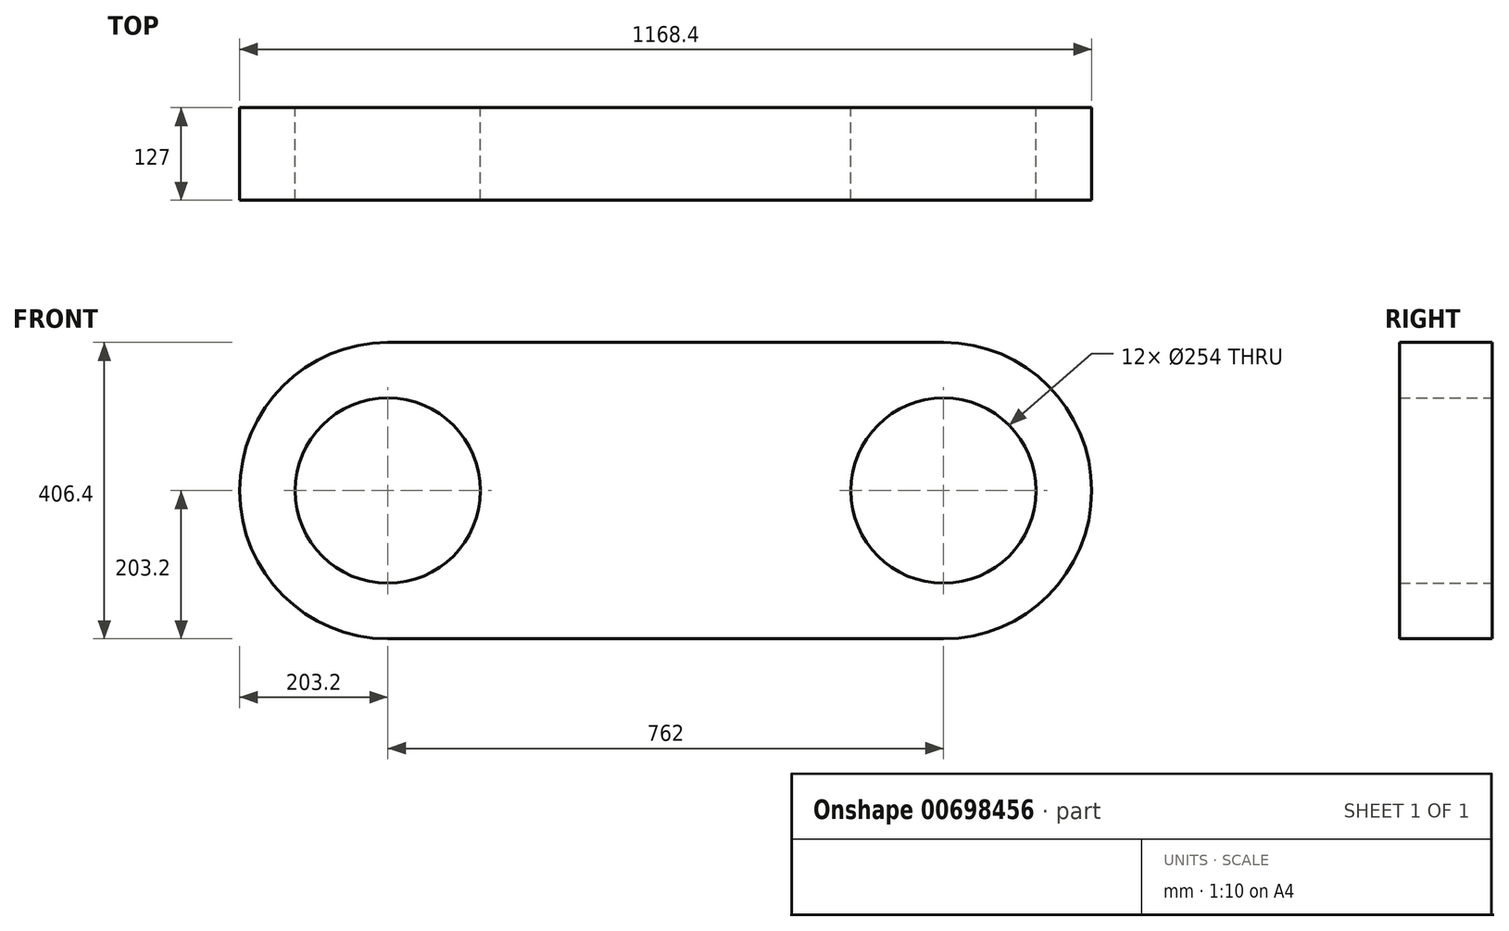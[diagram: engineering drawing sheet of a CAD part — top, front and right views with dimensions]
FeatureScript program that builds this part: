
annotation { "Feature Type Name" : "Feature", "Feature Type Description" : "" }
export const myFeature = defineFeature(function(context is Context, id is Id, definition is map)
    precondition{}
    {
        {
            var Q0;
            Q0=qCreatedBy(makeId("Front.planeOp"),FACE);
            var sketch = newSketch(context, id + "F0", { "sketchPlane" : qUnion([Q0])});
            skLineSegment(sketch, "E0.bottom", {"start": v(-381, 203.2) * mm, "end": v(381, 203.2) * mm});
            skLineSegment(sketch, "E0.top", {"start": v(-381, -203.2) * mm, "end": v(381, -203.2) * mm});
            skArc(sketch, "E1", {"start": v(-381, 203.2) * mm, "mid": v(-584.2, 0) * mm, "end": v(-381, -203.2) * mm});
            skArc(sketch, "E2", {"start": v(381, -203.2) * mm, "mid": v(584.2, 0) * mm, "end": v(381, 203.2) * mm});
            skCircle(sketch, "E3", {"center": v(381, 0) * mm, "radius": 127 * mm});
            skCircle(sketch, "E4", {"center": v(-381, 0) * mm, "radius": 127 * mm});
            skSolve(sketch);
        }
        {
            var Q0;
            Q0=qSketchRegion(id+"F0",true);
            extrude(context, id + "F1", {"entities" : qUnion([Q0]), "endBound" : BoundingType.SYMMETRIC, "depth" : 127 * mm, "offsetDistance" : 25.4 * mm});
        }
    });
